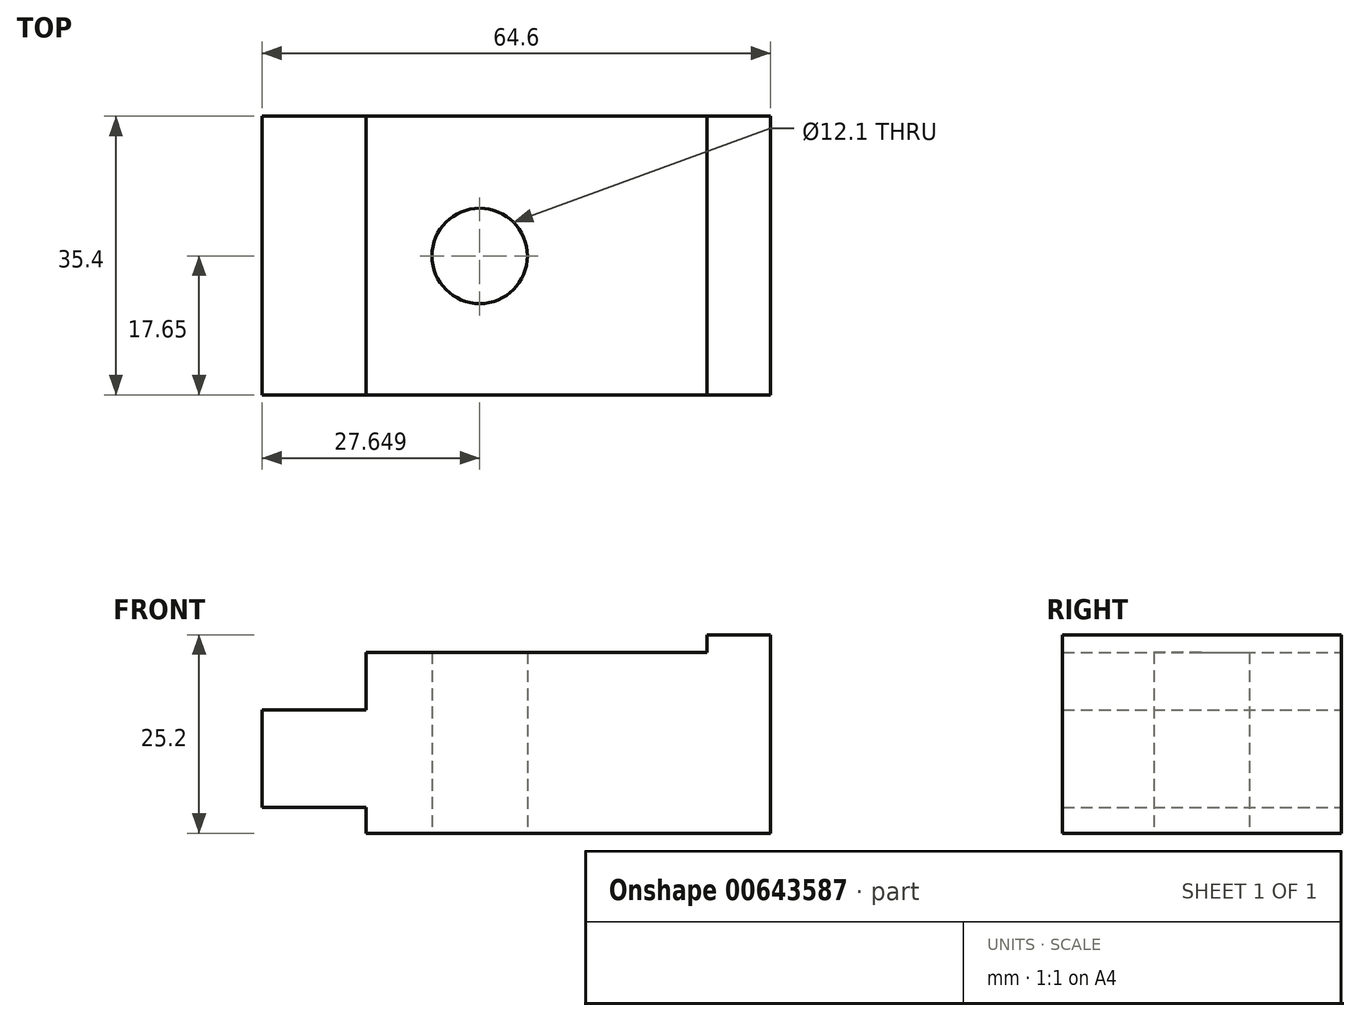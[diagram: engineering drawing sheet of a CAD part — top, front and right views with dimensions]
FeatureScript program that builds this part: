
annotation { "Feature Type Name" : "Feature", "Feature Type Description" : "" }
export const myFeature = defineFeature(function(context is Context, id is Id, definition is map)
    precondition{}
    {
        {
            var Q0;
            Q0=qCreatedBy(makeId("Front.planeOp"),FACE);
            var sketch = newSketch(context, id + "F0", { "sketchPlane" : qUnion([Q0])});
            skLineSegment(sketch, "E0", {"start": v(19.23, 16.28) * mm, "end": v(27.33, 16.28) * mm});
            skLineSegment(sketch, "E1", {"start": v(27.33, 16.28) * mm, "end": v(27.33, -8.92) * mm});
            skLineSegment(sketch, "E2", {"start": v(27.33, -8.92) * mm, "end": v(-24.07, -8.92) * mm});
            skLineSegment(sketch, "E3", {"start": v(-24.07, -5.62) * mm, "end": v(-37.27, -5.62) * mm});
            skLineSegment(sketch, "E4", {"start": v(-37.27, -5.62) * mm, "end": v(-37.27, 6.78) * mm});
            skLineSegment(sketch, "E5", {"start": v(-37.27, 6.78) * mm, "end": v(-24.07, 6.78) * mm});
            skLineSegment(sketch, "E6", {"start": v(-24.07, 6.78) * mm, "end": v(-24.07, 14.08) * mm});
            skLineSegment(sketch, "E7", {"start": v(-24.07, 14.08) * mm, "end": v(19.23, 14.08) * mm});
            skLineSegment(sketch, "E8", {"start": v(19.23, 16.28) * mm, "end": v(19.23, 14.08) * mm});
            skLineSegment(sketch, "E9", {"start": v(-24.07, -8.92) * mm, "end": v(-24.07, -5.62) * mm});
            skSolve(sketch);
        }
        {
            var Q0;
            Q0=makeQuery(id+"F0.imprint","IMPRINT",FACE,{"disambiguationData":[TD([[makeQuery(id+"F0.imprint","IMPRINT",EDGE,{"derivedFrom":sQuery(id+"F0.wireOp",EDGE,"E0")}),-1.0]])]});
            extrude(context, id + "F1", {"entities" : qUnion([Q0]), "depth" : 35.4 * mm, "offsetDistance" : 25.4 * mm});
        }
        {
            var Q0;
            Q0=qCreatedBy(makeId("Top.planeOp"),FACE);
            var sketch = newSketch(context, id + "F2", { "sketchPlane" : qUnion([Q0])});
            skCircle(sketch, "E10", {"center": v(-9.62, -17.75) * mm, "radius": 6.05 * mm});
            skSolve(sketch);
        }
        {
            var Q0;
            Q0=sQuery(id+"F2.wireOp",VERTEX,"E10.center");
            var Q1;
            Q1=makeQuery(id+"F1.opExtrude","SWEPT_BODY",BODY,{"disambiguationData":[OSD([sQuery(id+"F0.wireOp",EDGE,"E0"),sQuery(id+"F0.wireOp",EDGE,"E1"),sQuery(id+"F0.wireOp",EDGE,"E2"),sQuery(id+"F0.wireOp",EDGE,"E3"),sQuery(id+"F0.wireOp",EDGE,"E4"),sQuery(id+"F0.wireOp",EDGE,"E5"),sQuery(id+"F0.wireOp",EDGE,"E6"),sQuery(id+"F0.wireOp",EDGE,"E7"),sQuery(id+"F0.wireOp",EDGE,"E8"),sQuery(id+"F0.wireOp",EDGE,"E9")])]});
            hole(context, id + "F3", {"style" : HoleStyle.SIMPLE, "endStyle" : HoleEndStyle.THROUGH, "oppositeDirection" : true, "holeDiameter" : 12.1 * mm, "majorDiameter" : 6.35 * mm, "isTappedThrough" : true, "tappedDepth" : 12.7 * mm, "tapClearance" : 3, "locations" : qUnion([Q0]), "scope" : qUnion([Q1])});
        }
        {
            var Q0;
            Q0=sQuery(id+"F2.wireOp",VERTEX,"E10.center");
            var Q1;
            Q1=makeQuery(id+"F1.opExtrude","SWEPT_BODY",BODY,{"disambiguationData":[OSD([sQuery(id+"F0.wireOp",EDGE,"E0"),sQuery(id+"F0.wireOp",EDGE,"E1"),sQuery(id+"F0.wireOp",EDGE,"E2"),sQuery(id+"F0.wireOp",EDGE,"E3"),sQuery(id+"F0.wireOp",EDGE,"E4"),sQuery(id+"F0.wireOp",EDGE,"E5"),sQuery(id+"F0.wireOp",EDGE,"E6"),sQuery(id+"F0.wireOp",EDGE,"E7"),sQuery(id+"F0.wireOp",EDGE,"E8"),sQuery(id+"F0.wireOp",EDGE,"E9")])]});
            hole(context, id + "F4", {"style" : HoleStyle.SIMPLE, "endStyle" : HoleEndStyle.THROUGH, "holeDiameter" : 12.1 * mm, "majorDiameter" : 6.35 * mm, "isTappedThrough" : true, "tappedDepth" : 12.7 * mm, "tapClearance" : 3, "locations" : qUnion([Q0]), "scope" : qUnion([Q1])});
        }
    });
